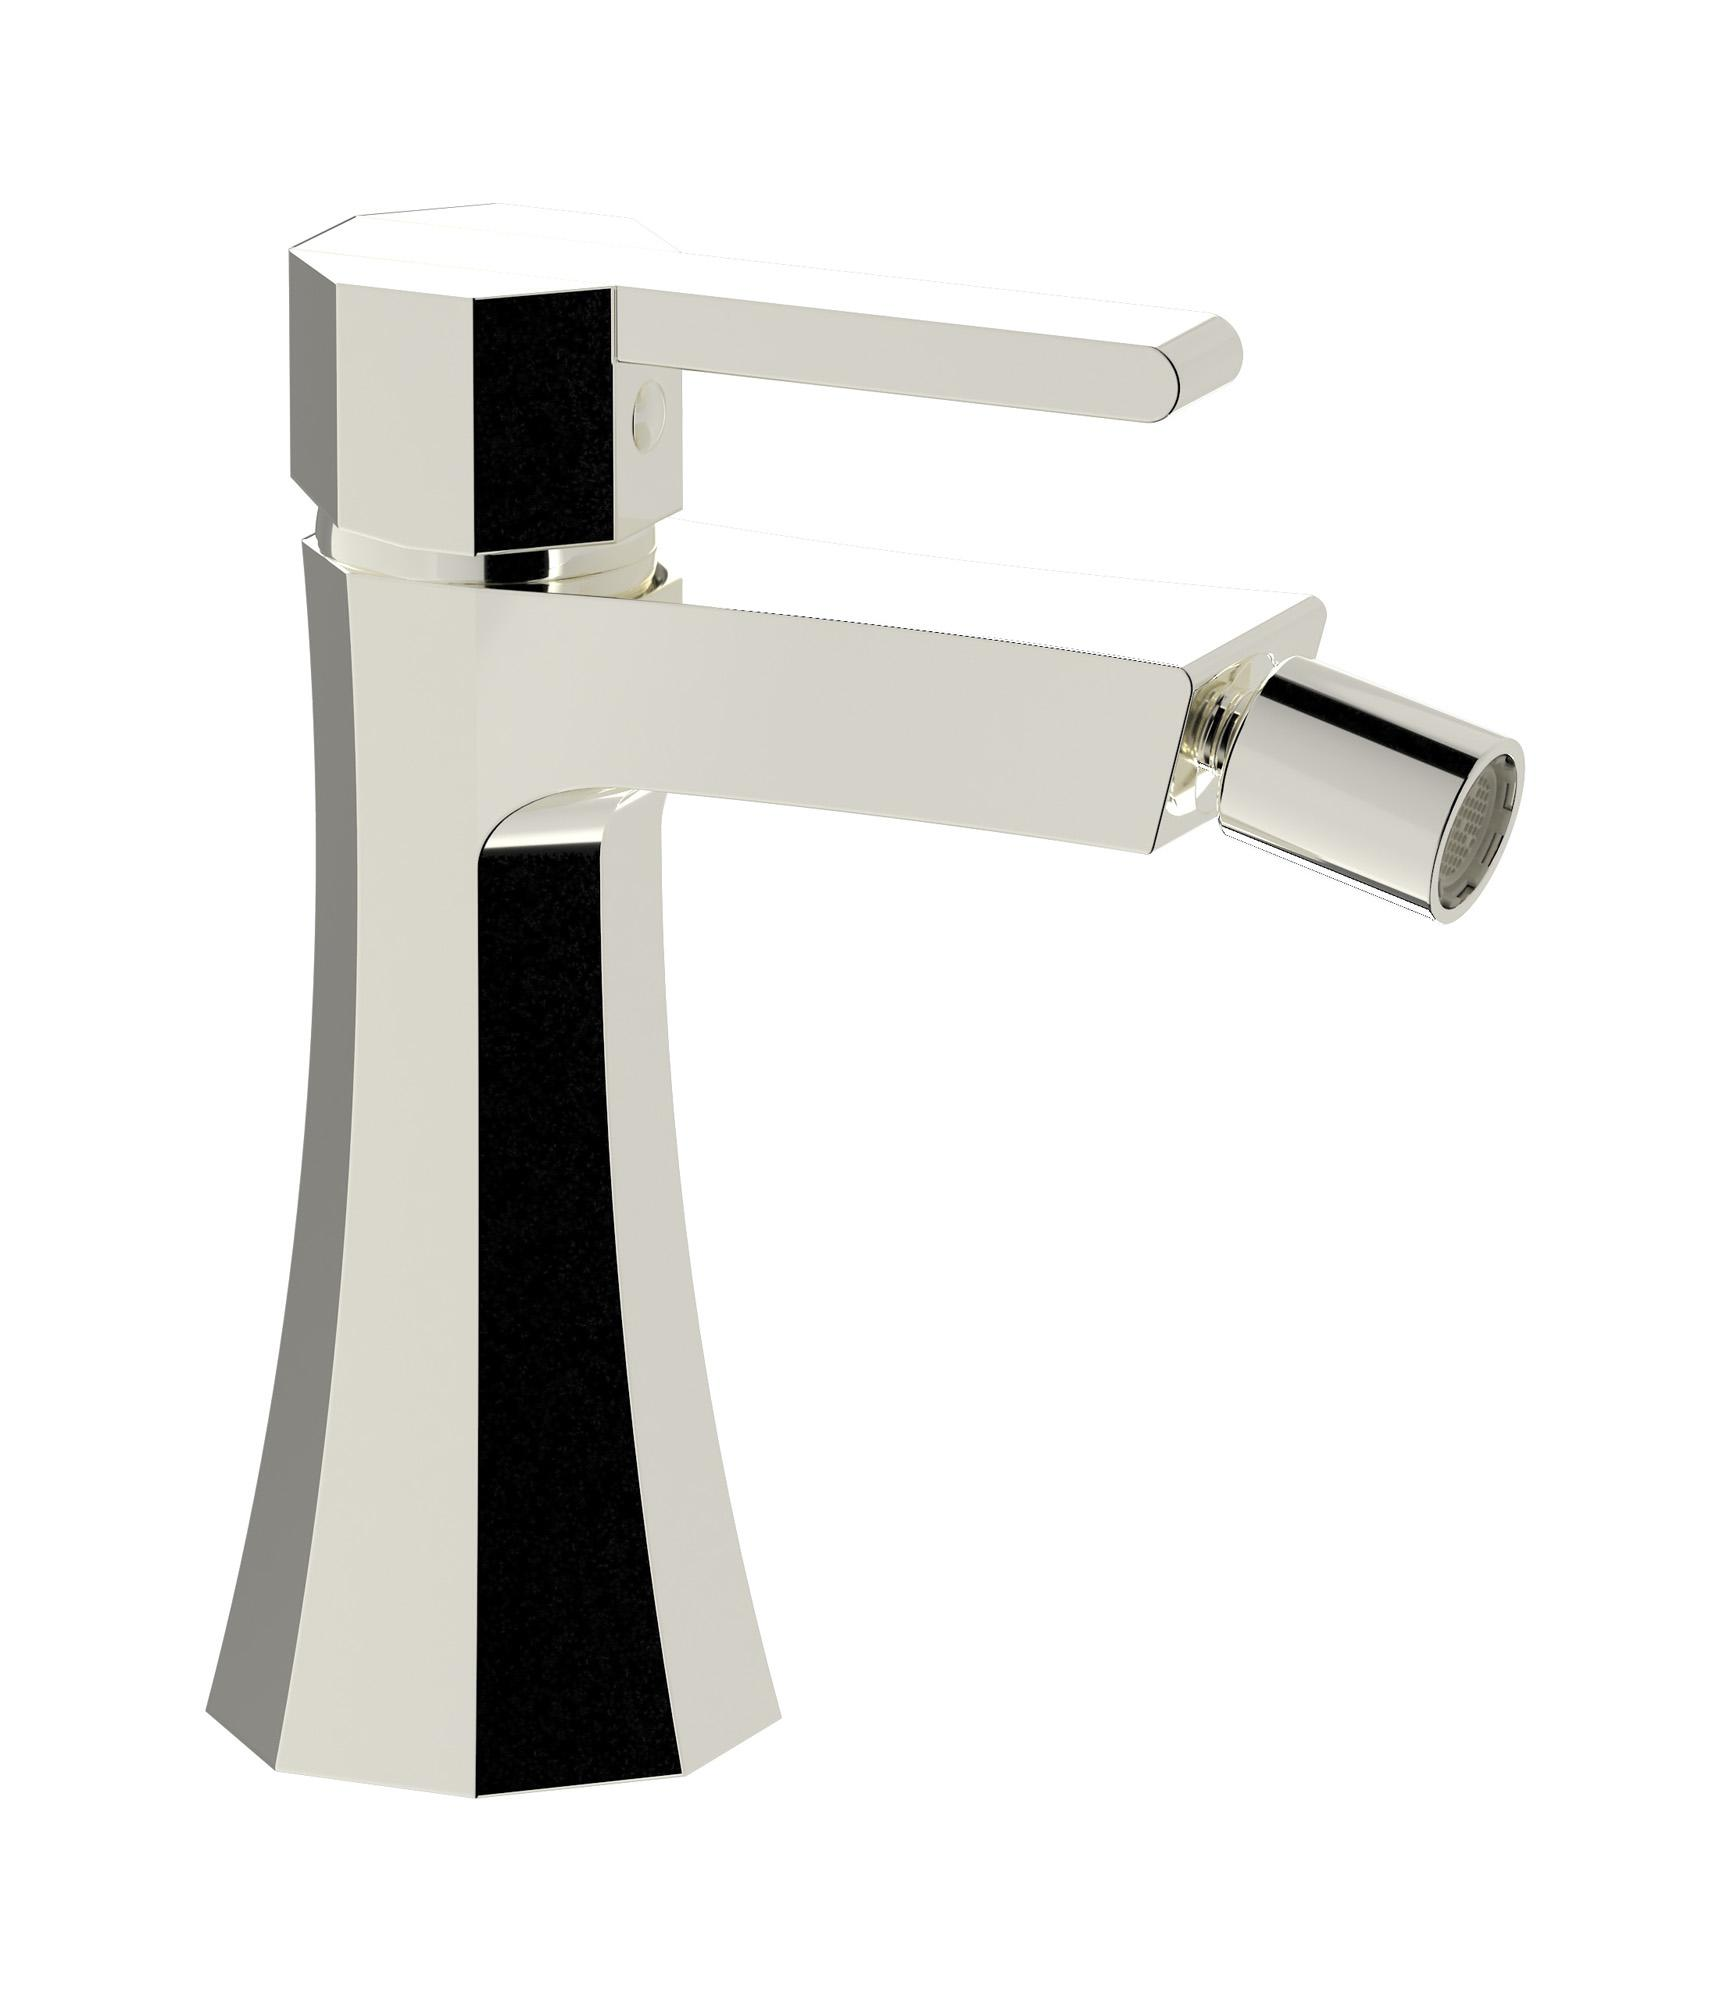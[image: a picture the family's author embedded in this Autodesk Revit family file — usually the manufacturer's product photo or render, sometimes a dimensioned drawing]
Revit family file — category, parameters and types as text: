
# Revit family: BL220
name_source: partatom
category: Apparecchi idraulici
units: mm (PartAtom-declared; Revit-internal decimal feet)

## family parameters
Basato su piano di lavoro = No
Condiviso = No
Mantieni orientamento annotazione = No
Numero OmniClass = 23.45.55.17
Punto di calcolo locali = No
Quota connettore circolare = Usa diametro
Sempre verticale = Sì
Taglio con vuoti quando caricato = No
Tipo di parte = Normale
Titolo OmniClass = Mixing Faucets

## types (7) — shared parameters
Cold water inlet = 10 mm  [stored 0.0328084 ft]
Commenti sul tipo = Monohole bidet mixer complete with drain
Connessione CW = No
Connessione HW = No
Connessione di scarico = No
Connessione di ventilazione = No
Descrizione = Monohole bidet mixer complete with drain
Hot water inlet = 10 mm  [stored 0.0328084 ft]
Produttore = IB Rubinetterie S.p.A.
URL = https://www.weareib.it
zero-valued in all types: Prospetto di default

## per-type parameters (varying)
| type | Finishes surface | Immagine tipo | Modello |
| Chrome | IB_Chrome | BL220CC.jpg | BL220CC |
| Pale Gold | IB_Pale gold | BL220II.jpg | BL220II |
| Modern Bronze | IB_Modern bronze | BL220MB.jpg | BL220MB |
| Gold | IB_gold | BL220OO.jpg | BL220OO |
| Platinum | IB_Platinum | BL220PL.jpg | BL220PL |
| Rose Gold | IB_Rose gold | BL220RS.jpg | BL220RS |
| Brushed Nickel | IB_Brushed nickel | BL220SS.jpg | BL220SS |

note: [stored X ft] marks values corroborated as IEEE doubles in the binary element streams (Revit-internal decimal feet)
